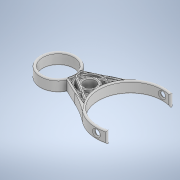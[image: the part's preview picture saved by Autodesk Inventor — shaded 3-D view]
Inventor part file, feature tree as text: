
AUTODESK INVENTOR PART (.ipt)
format: ipt  version: 2020 (Build 240168000, 168)  size: 640,512 bytes
history: native  units: in
note: dims shown in document units (in); Inventor stores cm internally (conversion verified against a paired STEP export)
features: fillet x5, extrude x2, sketch x2
ambient origin geometry x8: Origin, YZ Plane, XZ Plane, XY Plane, X Axis, Y Axis, Z Axis, Center Point
bodies: Solid1 (feature_tree)
feature tree (9):
  extrude  "Extrusion1"  Depth=0.1181in
  extrude  "Extrusion2"  Depth=1.4567in
  fillet  "Fillet2"  Radius=0.1181in
  fillet  "Fillet3"  Radius=0.2362in
  fillet  "Fillet4"  Radius=0.2362in
  fillet  "Fillet5"  Radius=0.5512in
  fillet  "Fillet6"  Radius=0.4331in
  sketch  "Sketch1"  dims[d0=2.9921in d1=0.1181in]
  sketch  "Sketch2"  dims[d2=1.1811in d3=1.4567in d4=0.1181in d5=0.2362in d6=0.2362in d7=0.5512in d8=0.0in d10=0.4331in d11=0.2402in d12=10.0in d13=0.0in d14=0.0591in d15=0.0591in d16=0.0394in d17=0.0394in d18=5.0in d9=0.5in]
